# Revit family: Pressure_Balance_Valve_Shower-GROHE-Concetto-102495_Series
name_source: partatom
category: Plumbing Fixtures
units: mm (PartAtom-declared; Revit-internal decimal feet)

## family parameters
Cut with Voids When Loaded = No
Host = Face
OmniClass Number = 23.45.05.14.17
OmniClass Title = Showers
Part Type = Normal
Room Calculation Point = No
Round Connector Dimension = Use Diameter
Shared = Yes

## types (3) — shared parameters
ADA Compliant = Yes
Assembly Code = D2010710
CEC Compliant = Yes
CW Connection = Yes
CWFU = 1.5
CalGreen Compliant = Yes
Cold Water Connection Diameter = 1/2"
Cold Water Connection Radius = 1/4"
Compliance Certifications = • Massachusetts Plumbing Board Approved
• Energy Policy Act of 1992
• CSA B125.1
• ASME A112.18.1
Concetto Pressure Balance Trim with Cartridge (14 468) = Yes
Default Elevation = 40"
Description = Concetto Bathtub/Shower Combo Faucet
Flow Rate = 2.0 gpm
HW Connection = Yes
HWFU = 1.5
Hot Water Connection Diameter = 1"
Hot Water Connection Radius = 1/4"
Installation Type = Wall Mounted
Manufacturer = Grohe
Relexa 5” Shower Arm (27 414) = Yes
Tempered Connection Diameter = 1/2"
Tempered Connection Radius = 1/4"
Tempesta Cosmo Shower Head 4-Sprays (26 043) = Yes
URL = https://www.grohe.com
Vent Connection = No
WFU = 2
Waste Connection = No

## per-type parameters (varying)
| type | Finish | Material |
| 1024950000 | Metal-Grohe-000-StarLight Chrome | Metal-Grohe-000-StarLight Chrome |
| 1024952430 | Metal-Grohe-2430-Matte Black | Metal-Grohe-2430-Matte Black |
| 102495EN00 | Metal-Grohe-EN0-Brushed Nickel Infinity Finish | Metal-Grohe-EN0-Brushed Nickel Infinity Finish |

note: column(s) folded — value = type name in every type: Model

## geometry (parser evidence)
native form markers: Sweep x3
no freeform markers — native parametric forms only
